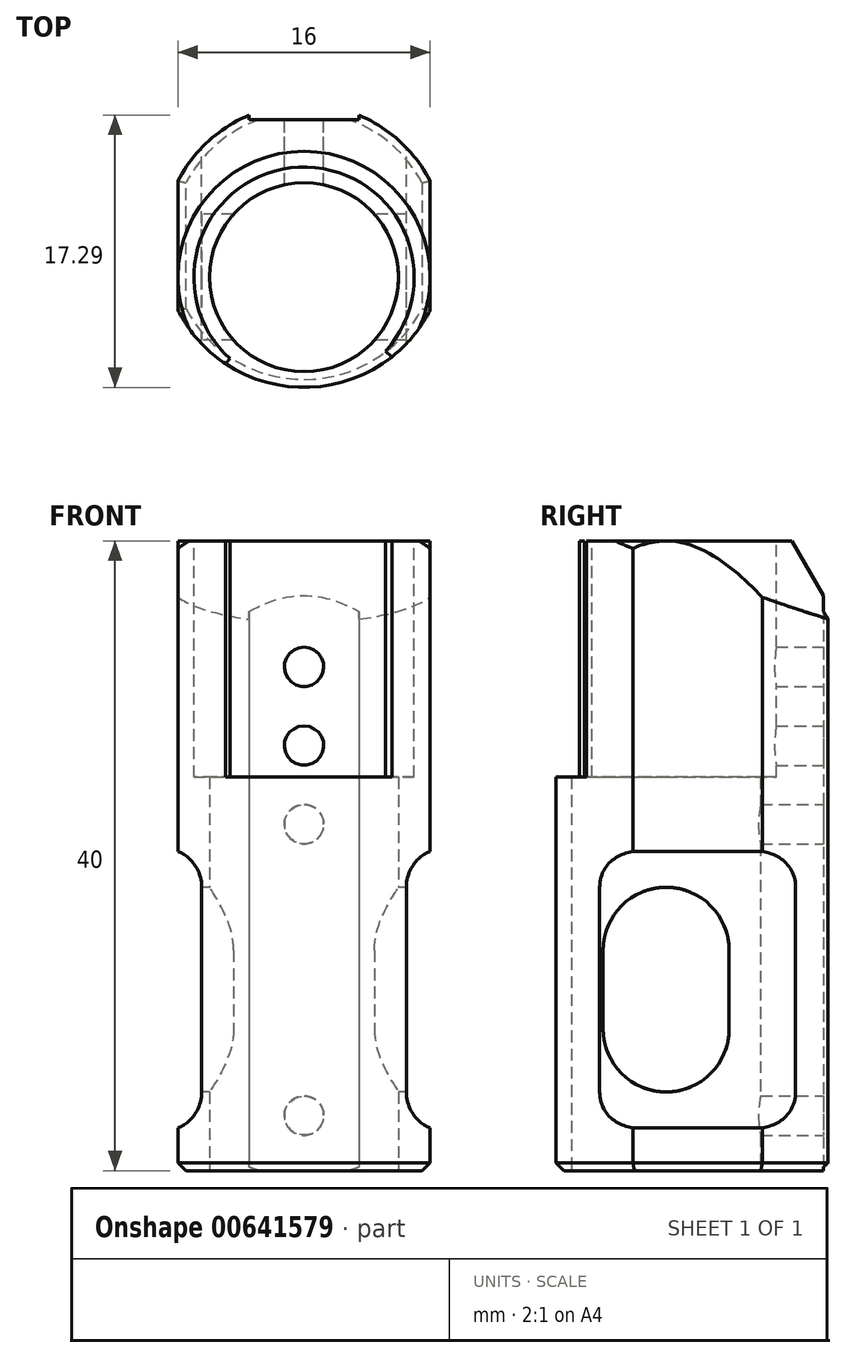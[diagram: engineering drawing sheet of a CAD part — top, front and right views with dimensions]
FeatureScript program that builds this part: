
annotation { "Feature Type Name" : "Feature", "Feature Type Description" : "" }
export const myFeature = defineFeature(function(context is Context, id is Id, definition is map)
    precondition{}
    {
        {
            var Q0;
            Q0=qCreatedBy(makeId("Top.planeOp"),FACE);
            var sketch = newSketch(context, id + "F0", { "sketchPlane" : qUnion([Q0])});
            skCircle(sketch, "E0", {"center": v(0, 0) * mm, "radius": 6 * mm});
            skArc(sketch, "E1", {"start": v(-8, -2.12) * mm, "mid": v(0, -7) * mm, "end": v(8, -2.12) * mm});
            skLineSegment(sketch, "E2.left", {"start": v(8, -2.12) * mm, "end": v(8, 6.12) * mm});
            skLineSegment(sketch, "E2.right", {"start": v(-8, -2.12) * mm, "end": v(-8, 6.12) * mm});
            skPoint(sketch, "E3.orphan", {"position": v(-8, 13.3) * mm});
            skPoint(sketch, "E2.bottom.end.orphan", {"position": v(-8, -13.3) * mm});
            skPoint(sketch, "E4.orphan", {"position": v(8, -13.3) * mm});
            skPoint(sketch, "E5.orphan", {"position": v(8, 13.3) * mm});
            skArc(sketch, "E6.trimOffspring", {"start": v(8, 6.12) * mm, "mid": v(6.12, 8.6) * mm, "end": v(3.5, 10.3) * mm});
            skLineSegment(sketch, "E7.bottom", {"start": v(3.5, 10) * mm, "end": v(-3.5, 10) * mm});
            skLineSegment(sketch, "E7.left", {"start": v(3.5, 10) * mm, "end": v(3.5, 10.3) * mm});
            skLineSegment(sketch, "E7.right", {"start": v(-3.5, 10) * mm, "end": v(-3.5, 10.3) * mm});
            skPoint(sketch, "E7.middle", {"position": v(0, 11) * mm});
            skPoint(sketch, "E8.orphan", {"position": v(3.5, 12) * mm});
            skArc(sketch, "E9.trimOffspring", {"start": v(-3.5, 10.3) * mm, "mid": v(-6.12, 8.6) * mm, "end": v(-8, 6.12) * mm});
            skPoint(sketch, "E10.orphan", {"position": v(-3.5, 12) * mm});
            skSolve(sketch);
        }
        {
            var Q0;
            Q0=makeQuery(id+"F0.imprint","IMPRINT",FACE,{"disambiguationData":[TD([[makeQuery(id+"F0.imprint","IMPRINT",EDGE,{"derivedFrom":sQuery(id+"F0.wireOp",EDGE,"E0")}),-1.0]])]});
            extrude(context, id + "F1", {"entities" : qUnion([Q0]), "depth" : 40 * mm, "offsetDistance" : 25 * mm});
        }
        {
            var Q0;
            Q0=makeQuery(id+"F1.opExtrude","CAP_FACE",FACE,{"disambiguationData":[OSD([sQuery(id+"F0.wireOp",EDGE,"E0"),sQuery(id+"F0.wireOp",EDGE,"E1"),sQuery(id+"F0.wireOp",EDGE,"E2.left"),sQuery(id+"F0.wireOp",EDGE,"E2.right"),sQuery(id+"F0.wireOp",EDGE,"E6.trimOffspring"),sQuery(id+"F0.wireOp",EDGE,"E7.bottom"),sQuery(id+"F0.wireOp",EDGE,"E7.left"),sQuery(id+"F0.wireOp",EDGE,"E7.right"),sQuery(id+"F0.wireOp",EDGE,"E9.trimOffspring")])],"isStart":false});
            var sketch = newSketch(context, id + "F2", { "sketchPlane" : qUnion([Q0])});
            skCircle(sketch, "E11", {"center": v(0, 0) * mm, "radius": 7 * mm});
            skLineSegment(sketch, "E12", {"start": v(0, 0) * mm, "end": v(-4.99, -5.5) * mm});
            skLineSegment(sketch, "E13", {"start": v(0, 0) * mm, "end": v(5.58, -5.06) * mm});
            skLineSegment(sketch, "E14", {"start": v(0, 0) * mm, "end": v(0, -8.98) * mm, "construction": true});
            skSolve(sketch);
        }
        {
            var Q0;
            {var subQ0=sQuery(id+"F2.wireOp",EDGE,"E12");var subQ1=sQuery(id+"F2.wireOp",EDGE,"E11");var subQ2=makeQuery(id+"F2.imprint","INTERSECT",VERTEX,{"derivedFrom":[subQ1,subQ0]});Q0=makeQuery(id+"F2.imprint","IMPRINT",FACE,{"disambiguationData":[TD([[makeQuery(id+"F2.imprint","IMPRINT",EDGE,{"disambiguationData":[TD([[subQ2,1.0]])],"derivedFrom":subQ1}),1.0]])]});}
            var Q1;
            {var subQ1=sQuery(id+"F2.wireOp",EDGE,"E11");var subQ5=sQuery(id+"F2.wireOp",EDGE,"E12");var subQ6=makeQuery(id+"F2.imprint","INTERSECT",VERTEX,{"derivedFrom":[subQ1,subQ5]});Q1=makeQuery(id+"F2.imprint","IMPRINT",FACE,{"disambiguationData":[TD([[makeQuery(id+"F2.imprint","IMPRINT",EDGE,{"disambiguationData":[TD([[subQ6,-1.0]])],"derivedFrom":subQ1}),1.0]])]});}
            var Q2;
            {var subQ0=sQuery(id+"F2.wireOp",EDGE,"E12");var subQ1=sQuery(id+"F2.wireOp",EDGE,"E11");var subQ2=makeQuery(id+"F2.imprint","INTERSECT",VERTEX,{"derivedFrom":[subQ1,subQ0]});Q2=makeQuery(id+"F2.imprint","IMPRINT",FACE,{"disambiguationData":[TD([[makeQuery(id+"F2.imprint","IMPRINT",EDGE,{"disambiguationData":[TD([[subQ2,-1.0]])],"derivedFrom":subQ1}),-1.0]])]});}
            var Q3;
            {var subQ0=sQuery(id+"F2.wireOp",EDGE,"E13");var subQ1=sQuery(id+"F2.wireOp",EDGE,"E11");var subQ2=makeQuery(id+"F2.imprint","INTERSECT",VERTEX,{"derivedFrom":[subQ1,subQ0]});Q3=makeQuery(id+"F2.imprint","IMPRINT",FACE,{"disambiguationData":[TD([[makeQuery(id+"F2.imprint","IMPRINT",EDGE,{"disambiguationData":[TD([[subQ2,1.0]])],"derivedFrom":subQ1}),-1.0]])]});}
            extrude(context, id + "F3", {"entities" : qUnion([Q0, Q1, Q2, Q3]), "operationType" : NewBodyOperationType.REMOVE, "oppositeDirection" : true, "depth" : 15 * mm, "offsetDistance" : 25 * mm});
        }
        {
            var Q0;
            Q0=qCreatedBy(makeId("Front.planeOp"),FACE);
            var sketch = newSketch(context, id + "F4", { "sketchPlane" : qUnion([Q0])});
            skLineSegment(sketch, "E15", {"start": v(0, 0) * mm, "end": v(0, 54) * mm, "construction": true});
            skPoint(sketch, "E16.0", {"position": v(8, 40) * mm});
            skLineSegment(sketch, "E17", {"start": v(0, 54) * mm, "end": v(0, 53.86) * mm});
            skLineSegment(sketch, "E18", {"start": v(8, 40) * mm, "end": v(14.67, 28.45) * mm});
            skLineSegment(sketch, "E19", {"start": v(14.67, 28.45) * mm, "end": v(14.67, 47.25) * mm});
            skLineSegment(sketch, "E20", {"start": v(14.67, 47.25) * mm, "end": v(0, 47.25) * mm});
            skLineSegment(sketch, "E21", {"start": v(0, 47.25) * mm, "end": v(0, 44.06) * mm});
            skLineSegment(sketch, "E22", {"start": v(0, 44.06) * mm, "end": v(8, 40) * mm});
            skSolve(sketch);
        }
        {
            var Q0;
            Q0=makeQuery(id+"F4.imprint","IMPRINT",FACE,{"disambiguationData":[TD([[makeQuery(id+"F4.imprint","IMPRINT",EDGE,{"derivedFrom":sQuery(id+"F4.wireOp",EDGE,"E18")}),1.0]])]});
            var Q1;
            Q1=sQuery(id+"F4.wireOp",EDGE,"E15");
            revolve(context, id + "F5", {"operationType" : NewBodyOperationType.REMOVE, "surfaceOperationType" : NewSurfaceOperationType.NEW, "entities" : qUnion([Q0]), "axis" : qUnion([Q1]), "revolveType" : RevolveType.FULL});
        }
        {
            var Q0;
            Q0=makeQuery(id+"F1.opExtrude","CAP_EDGE",EDGE,{"disambiguationData":[OSD([sQuery(id+"F0.wireOp",EDGE,"E6.trimOffspring")])],"isStart":true});
            var Q1;
            Q1=makeQuery(id+"F1.opExtrude","CAP_EDGE",EDGE,{"disambiguationData":[OSD([sQuery(id+"F0.wireOp",EDGE,"E9.trimOffspring")])],"isStart":true});
            var Q2;
            Q2=makeQuery(id+"F1.opExtrude","CAP_EDGE",EDGE,{"disambiguationData":[OSD([sQuery(id+"F0.wireOp",EDGE,"E2.right")])],"isStart":true});
            var Q3;
            Q3=makeQuery(id+"F1.opExtrude","CAP_EDGE",EDGE,{"disambiguationData":[OSD([sQuery(id+"F0.wireOp",EDGE,"E1")])],"isStart":true});
            var Q4;
            Q4=makeQuery(id+"F1.opExtrude","CAP_EDGE",EDGE,{"disambiguationData":[OSD([sQuery(id+"F0.wireOp",EDGE,"E2.left")])],"isStart":true});
            chamfer(context, id + "F6", {"entities" : qUnion([Q0, Q1, Q2, Q3, Q4]), "width" : 0.5 * mm, "tangentPropagation" : true});
        }
        {
            var Q0;
            Q0=makeQuery(id+"F1.opExtrude","SWEPT_FACE",FACE,{"disambiguationData":[OSD([sQuery(id+"F0.wireOp",EDGE,"E2.right")])]});
            var sketch = newSketch(context, id + "F7", { "sketchPlane" : qUnion([Q0])});
            skLineSegment(sketch, "E23", {"start": v(0, -9.18) * mm, "end": v(0, 64.15) * mm, "construction": true});
            skCircle(sketch, "E24", {"center": v(0, 9) * mm, "radius": 4 * mm});
            skCircle(sketch, "E25", {"center": v(0, 14) * mm, "radius": 4 * mm});
            skLineSegment(sketch, "E26", {"start": v(-4, 9) * mm, "end": v(4, 9) * mm, "construction": true});
            skLineSegment(sketch, "E27", {"start": v(-4, 14) * mm, "end": v(4, 14) * mm, "construction": true});
            skLineSegment(sketch, "E28", {"start": v(-4, 14) * mm, "end": v(-4, 9) * mm});
            skLineSegment(sketch, "E29", {"start": v(4, 14) * mm, "end": v(4, 9) * mm});
            skSolve(sketch);
        }
        {
            var Q0;
            {var subQ0=sQuery(id+"F7.wireOp",EDGE,"Whs55cGE-NpJL-e0Uf-47Bt-mfnLZQVnPiic");var subQ1=sQuery(id+"F7.wireOp",EDGE,"E24");var subQ2=makeQuery(id+"F7.imprint","INTERSECT",VERTEX,{"derivedFrom":[subQ1,sQuery(id+"F7.wireOp",EDGE,"P3t80ODG-mQEx-n0Qn-k8V3-GYFliunrq4DK"),subQ0]});Q0=makeQuery(id+"F7.imprint","IMPRINT",FACE,{"disambiguationData":[TD([[makeQuery(id+"F7.imprint","IMPRINT",EDGE,{"disambiguationData":[TD([[subQ2,-1.0]])],"derivedFrom":subQ1}),1.0]])]});}
            var Q1;
            {var subQ1=sQuery(id+"F7.wireOp",EDGE,"P3t80ODG-mQEx-n0Qn-k8V3-GYFliunrq4DK");var subQ2=sQuery(id+"F7.wireOp",EDGE,"E24");var subQ8=makeQuery(id+"F7.imprint","INTERSECT",VERTEX,{"derivedFrom":[subQ2,subQ1]});Q1=makeQuery(id+"F7.imprint","IMPRINT",FACE,{"disambiguationData":[TD([[makeQuery(id+"F7.imprint","IMPRINT",EDGE,{"disambiguationData":[TD([[subQ8,1.0]])],"derivedFrom":subQ2}),1.0]])]});}
            var Q2;
            {var subQ0=sQuery(id+"F7.wireOp",EDGE,"E25");var subQ1=sQuery(id+"F7.wireOp",EDGE,"E24");var subQ2=makeQuery(id+"F7.imprint","INTERSECT",VERTEX,{"disambiguationData":[OD(0.0)],"derivedFrom":[subQ1,subQ0]});Q2=makeQuery(id+"F7.imprint","IMPRINT",FACE,{"disambiguationData":[TD([[makeQuery(id+"F7.imprint","IMPRINT",EDGE,{"disambiguationData":[TD([[subQ2,1.0]])],"derivedFrom":subQ1}),1.0]])]});}
            var Q3;
            {var subQ2=sQuery(id+"F7.wireOp",EDGE,"E25");var subQ6=sQuery(id+"F7.wireOp",EDGE,"E24");var subQ7=makeQuery(id+"F7.imprint","INTERSECT",VERTEX,{"disambiguationData":[OD(0.0)],"derivedFrom":[subQ6,subQ2]});Q3=makeQuery(id+"F7.imprint","IMPRINT",FACE,{"disambiguationData":[TD([[makeQuery(id+"F7.imprint","IMPRINT",EDGE,{"disambiguationData":[TD([[subQ7,1.0]])],"derivedFrom":subQ2}),1.0]])]});}
            var Q4;
            {var subQ0=sQuery(id+"F7.wireOp",EDGE,"EXD4O0jD-Jz0K-wQkZ-r5HG-xKK7gm0VS9MC");var subQ1=sQuery(id+"F7.wireOp",EDGE,"E25");var subQ2=makeQuery(id+"F7.imprint","INTERSECT",VERTEX,{"derivedFrom":[subQ1,sQuery(id+"F7.wireOp",EDGE,"P3t80ODG-mQEx-n0Qn-k8V3-GYFliunrq4DK"),subQ0]});Q4=makeQuery(id+"F7.imprint","IMPRINT",FACE,{"disambiguationData":[TD([[makeQuery(id+"F7.imprint","IMPRINT",EDGE,{"disambiguationData":[TD([[subQ2,1.0]])],"derivedFrom":subQ1}),1.0]])]});}
            var Q5;
            {var subQ0=sQuery(id+"F7.wireOp",EDGE,"EXD4O0jD-Jz0K-wQkZ-r5HG-xKK7gm0VS9MC");var subQ1=sQuery(id+"F7.wireOp",EDGE,"E25");var subQ2=makeQuery(id+"F7.imprint","INTERSECT",VERTEX,{"derivedFrom":[subQ1,subQ0,sQuery(id+"F7.wireOp",EDGE,"Wx670Ff3-3rKH-gHiv-3zdi-WdZotOS5Au2b")]});Q5=makeQuery(id+"F7.imprint","IMPRINT",FACE,{"disambiguationData":[TD([[makeQuery(id+"F7.imprint","IMPRINT",EDGE,{"disambiguationData":[TD([[subQ2,-1.0]])],"derivedFrom":subQ1}),1.0]])]});}
            var Q6;
            {var subQ0=sQuery(id+"F7.wireOp",EDGE,"Wx670Ff3-3rKH-gHiv-3zdi-WdZotOS5Au2b");var subQ2=sQuery(id+"F7.wireOp",EDGE,"E25");var subQ6=makeQuery(id+"F7.imprint","INTERSECT",VERTEX,{"derivedFrom":[subQ2,subQ0]});Q6=makeQuery(id+"F7.imprint","IMPRINT",FACE,{"disambiguationData":[TD([[makeQuery(id+"F7.imprint","IMPRINT",EDGE,{"disambiguationData":[TD([[subQ6,1.0]])],"derivedFrom":subQ2}),1.0]])]});}
            var Q7;
            {var subQ0=sQuery(id+"F7.wireOp",EDGE,"E25");var subQ1=sQuery(id+"F7.wireOp",EDGE,"E24");var subQ2=makeQuery(id+"F7.imprint","INTERSECT",VERTEX,{"disambiguationData":[OD(1.0)],"derivedFrom":[subQ1,subQ0]});Q7=makeQuery(id+"F7.imprint","IMPRINT",FACE,{"disambiguationData":[TD([[makeQuery(id+"F7.imprint","IMPRINT",EDGE,{"disambiguationData":[TD([[subQ2,-1.0]])],"derivedFrom":subQ1}),1.0]])]});}
            var Q8;
            {var subQ0=sQuery(id+"F7.wireOp",EDGE,"Wx670Ff3-3rKH-gHiv-3zdi-WdZotOS5Au2b");var subQ3=sQuery(id+"F7.wireOp",EDGE,"E25");var subQ5=makeQuery(id+"F7.imprint","INTERSECT",VERTEX,{"derivedFrom":[subQ3,subQ0]});Q8=makeQuery(id+"F7.imprint","IMPRINT",FACE,{"disambiguationData":[TD([[makeQuery(id+"F7.imprint","IMPRINT",EDGE,{"disambiguationData":[TD([[subQ5,1.0]])],"derivedFrom":subQ3}),-1.0]])]});}
            var Q9;
            {var subQ1=sQuery(id+"F7.wireOp",EDGE,"E24");var subQ3=sQuery(id+"F7.wireOp",EDGE,"E25");var subQ4=makeQuery(id+"F7.imprint","INTERSECT",VERTEX,{"disambiguationData":[OD(1.0)],"derivedFrom":[subQ1,subQ3]});Q9=makeQuery(id+"F7.imprint","IMPRINT",FACE,{"disambiguationData":[TD([[makeQuery(id+"F7.imprint","IMPRINT",EDGE,{"disambiguationData":[TD([[subQ4,1.0]])],"derivedFrom":subQ1}),1.0]])]});}
            var Q10;
            {var subQ0=sQuery(id+"F7.wireOp",EDGE,"Whs55cGE-NpJL-e0Uf-47Bt-mfnLZQVnPiic");var subQ1=sQuery(id+"F7.wireOp",EDGE,"E24");var subQ2=makeQuery(id+"F7.imprint","INTERSECT",VERTEX,{"derivedFrom":[subQ1,sQuery(id+"F7.wireOp",EDGE,"Wx670Ff3-3rKH-gHiv-3zdi-WdZotOS5Au2b"),subQ0]});Q10=makeQuery(id+"F7.imprint","IMPRINT",FACE,{"disambiguationData":[TD([[makeQuery(id+"F7.imprint","IMPRINT",EDGE,{"disambiguationData":[TD([[subQ2,1.0]])],"derivedFrom":subQ1}),1.0]])]});}
            var Q11;
            {var subQ0=sQuery(id+"F7.wireOp",EDGE,"P3t80ODG-mQEx-n0Qn-k8V3-GYFliunrq4DK");var subQ1=sQuery(id+"F7.wireOp",EDGE,"E24");var subQ2=makeQuery(id+"F7.imprint","INTERSECT",VERTEX,{"derivedFrom":[subQ1,subQ0]});Q11=makeQuery(id+"F7.imprint","IMPRINT",FACE,{"disambiguationData":[TD([[makeQuery(id+"F7.imprint","IMPRINT",EDGE,{"disambiguationData":[TD([[subQ2,1.0]])],"derivedFrom":subQ1}),-1.0]])]});}
            extrude(context, id + "F8", {"entities" : qUnion([Q0, Q1, Q2, Q3, Q4, Q5, Q6, Q7, Q8, Q9, Q10, Q11]), "operationType" : NewBodyOperationType.REMOVE, "endBound" : BoundingType.THROUGH_ALL, "oppositeDirection" : true, "depth" : 25 * mm, "offsetDistance" : 25 * mm});
        }
        {
            var Q0;
            Q0=makeQuery(id+"F1.opExtrude","SWEPT_FACE",FACE,{"disambiguationData":[OSD([sQuery(id+"F0.wireOp",EDGE,"E7.bottom")])]});
            var sketch = newSketch(context, id + "F9", { "sketchPlane" : qUnion([Q0])});
            skCircle(sketch, "E30", {"center": v(0, 3.5) * mm, "radius": 1.25 * mm});
            skPoint(sketch, "E30.centerSnap0", {"position": v(0, 0) * mm});
            skCircle(sketch, "E31", {"center": v(0, 27) * mm, "radius": 1.25 * mm});
            skCircle(sketch, "E32", {"center": v(0, 22) * mm, "radius": 1.25 * mm});
            skLineSegment(sketch, "E33", {"start": v(0, 36.54) * mm, "end": v(0, 0) * mm, "construction": true});
            skCircle(sketch, "E34", {"center": v(0, 32) * mm, "radius": 1.25 * mm});
            skLineSegment(sketch, "E35.bottom", {"start": v(6.5, 2.5) * mm, "end": v(-6.5, 2.5) * mm, "construction": true});
            skLineSegment(sketch, "E35.top", {"start": v(6.5, 20.5) * mm, "end": v(-6.5, 20.5) * mm, "construction": true});
            skLineSegment(sketch, "E35.left", {"start": v(6.5, 2.5) * mm, "end": v(6.5, 18) * mm, "construction": true});
            skLineSegment(sketch, "E35.right", {"start": v(-6.5, 2.5) * mm, "end": v(-6.5, 18) * mm, "construction": true});
            skPoint(sketch, "E35.middle", {"position": v(0, 11.5) * mm});
            skLineSegment(sketch, "E36.bottom", {"start": v(-9, 20.5) * mm, "end": v(-9.5, 20.5) * mm});
            skLineSegment(sketch, "E36.top", {"start": v(-9, 2.5) * mm, "end": v(-9.5, 2.5) * mm});
            skLineSegment(sketch, "E36.left", {"start": v(-6.5, 20.5) * mm, "end": v(-6.5, 5) * mm});
            skLineSegment(sketch, "E36.right", {"start": v(-9.5, 20.5) * mm, "end": v(-9.5, 2.5) * mm});
            skLineSegment(sketch, "E37.bottom", {"start": v(9, 20.5) * mm, "end": v(10.5, 20.5) * mm});
            skLineSegment(sketch, "E37.top", {"start": v(9, 2.5) * mm, "end": v(10.5, 2.5) * mm});
            skLineSegment(sketch, "E37.left", {"start": v(6.5, 20.5) * mm, "end": v(6.5, 5) * mm});
            skLineSegment(sketch, "E37.right", {"start": v(10.5, 20.5) * mm, "end": v(10.5, 2.5) * mm});
            skPoint(sketch, "E38.visualSharp", {"position": v(-6.5, 20.5) * mm});
            skArc(sketch, "E38.filletArc", {"start": v(-6.5, 18) * mm, "mid": v(-7.23, 19.77) * mm, "end": v(-9, 20.5) * mm});
            skPoint(sketch, "E39.visualSharp", {"position": v(6.5, 20.5) * mm});
            skArc(sketch, "E39.filletArc", {"start": v(9, 20.5) * mm, "mid": v(7.23, 19.77) * mm, "end": v(6.5, 18) * mm});
            skPoint(sketch, "E40.visualSharp", {"position": v(6.5, 2.5) * mm});
            skArc(sketch, "E40.filletArc", {"start": v(6.5, 5) * mm, "mid": v(7.23, 3.23) * mm, "end": v(9, 2.5) * mm});
            skPoint(sketch, "E41.visualSharp", {"position": v(-6.5, 2.5) * mm});
            skArc(sketch, "E41.filletArc", {"start": v(-9, 2.5) * mm, "mid": v(-7.23, 3.23) * mm, "end": v(-6.5, 5) * mm});
            skSolve(sketch);
        }
        {
            var Q0;
            Q0=makeQuery(id+"F9.imprint","IMPRINT",FACE,{"disambiguationData":[TD([[makeQuery(id+"F9.imprint","IMPRINT",EDGE,{"derivedFrom":sQuery(id+"F9.wireOp",EDGE,"E30")}),1.0]])]});
            var Q1;
            Q1=makeQuery(id+"F9.imprint","IMPRINT",FACE,{"disambiguationData":[TD([[makeQuery(id+"F9.imprint","IMPRINT",EDGE,{"derivedFrom":sQuery(id+"F9.wireOp",EDGE,"E32")}),1.0]])]});
            var Q2;
            Q2=makeQuery(id+"F9.imprint","IMPRINT",FACE,{"disambiguationData":[TD([[makeQuery(id+"F9.imprint","IMPRINT",EDGE,{"derivedFrom":sQuery(id+"F9.wireOp",EDGE,"E31")}),1.0]])]});
            var Q3;
            Q3=makeQuery(id+"F9.imprint","IMPRINT",FACE,{"disambiguationData":[TD([[makeQuery(id+"F9.imprint","IMPRINT",EDGE,{"derivedFrom":sQuery(id+"F9.wireOp",EDGE,"E34")}),1.0]])]});
            extrude(context, id + "F10", {"entities" : qUnion([Q0, Q1, Q2, Q3]), "operationType" : NewBodyOperationType.REMOVE, "endBound" : BoundingType.UP_TO_NEXT, "oppositeDirection" : true, "depth" : 25 * mm, "offsetDistance" : 25 * mm});
        }
        {
            var Q0;
            Q0=makeQuery(id+"F9.imprint","IMPRINT",FACE,{"disambiguationData":[TD([[makeQuery(id+"F9.imprint","IMPRINT",EDGE,{"derivedFrom":sQuery(id+"F9.wireOp",EDGE,"E36.bottom")}),1.0]])]});
            var Q1;
            Q1=makeQuery(id+"F9.imprint","IMPRINT",FACE,{"disambiguationData":[TD([[makeQuery(id+"F9.imprint","IMPRINT",EDGE,{"derivedFrom":sQuery(id+"F9.wireOp",EDGE,"E37.bottom")}),-1.0]])]});
            extrude(context, id + "F11", {"entities" : qUnion([Q0, Q1]), "operationType" : NewBodyOperationType.REMOVE, "oppositeDirection" : true, "depth" : 15 * mm, "offsetDistance" : 25 * mm});
        }
    });
